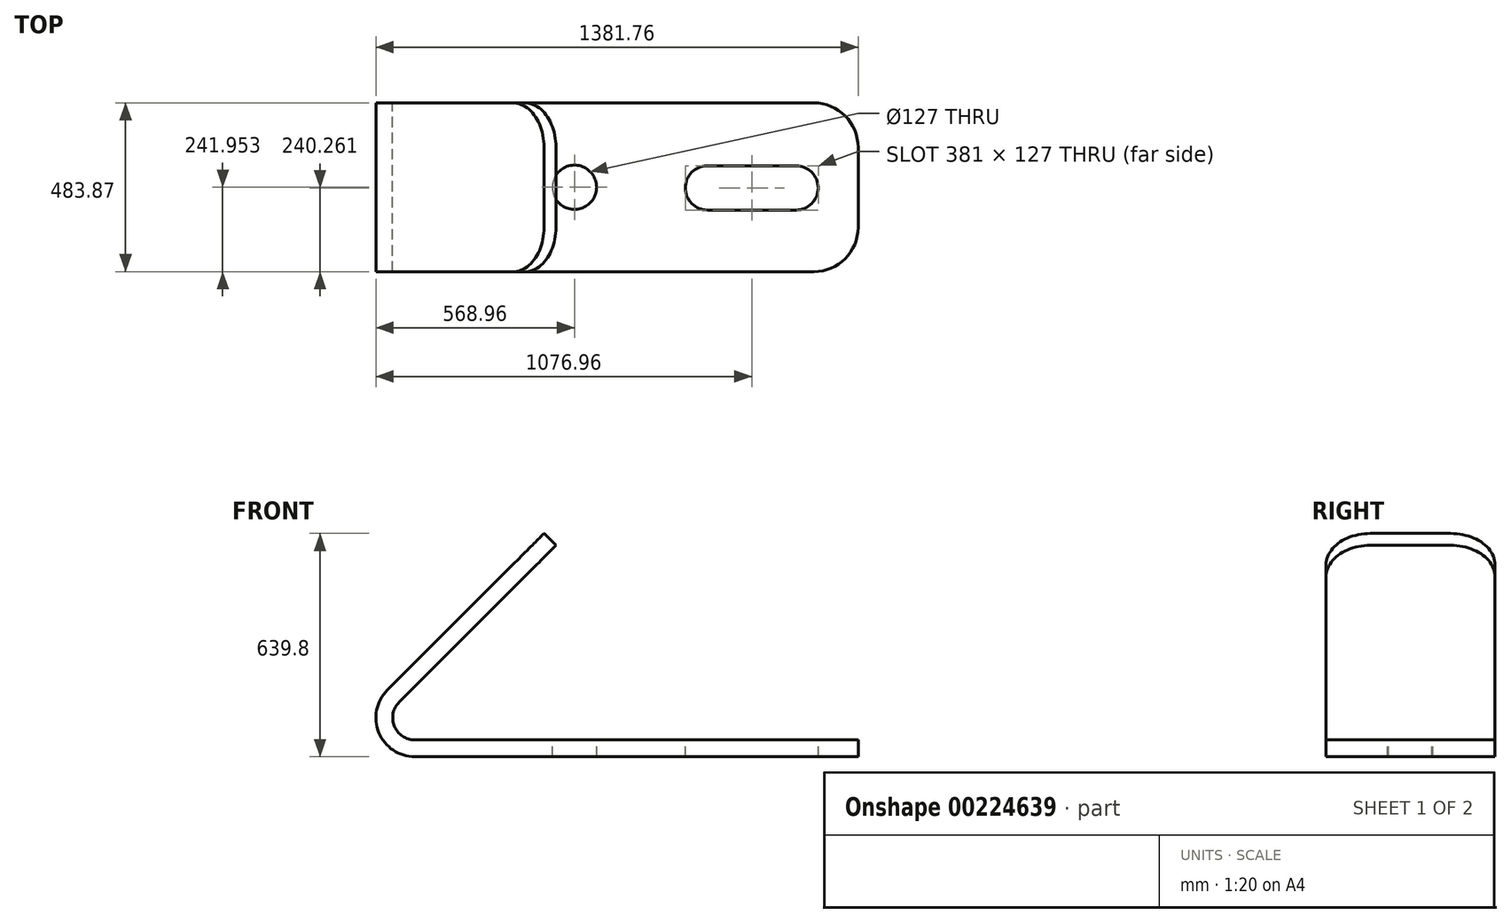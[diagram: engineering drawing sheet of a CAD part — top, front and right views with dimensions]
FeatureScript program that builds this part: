
annotation { "Feature Type Name" : "Feature", "Feature Type Description" : "" }
export const myFeature = defineFeature(function(context is Context, id is Id, definition is map)
    precondition{}
    {
        {
            var Q0;
            Q0=qCreatedBy(makeId("Front.planeOp"),FACE);
            var sketch = newSketch(context, id + "F0", { "sketchPlane" : qUnion([Q0])});
            skLineSegment(sketch, "E0", {"start": v(0, 0) * mm, "end": v(-1270, 0) * mm});
            skLineSegment(sketch, "E1", {"start": v(0, 0) * mm, "end": v(0, 48.26) * mm});
            skLineSegment(sketch, "E2", {"start": v(-1270, 48.26) * mm, "end": v(0, 48.26) * mm});
            skLineSegment(sketch, "E3", {"start": v(-1349.03, 190.79) * mm, "end": v(-900.01, 639.8) * mm});
            skArc(sketch, "E4", {"start": v(-1270, 0) * mm, "mid": v(-1373.25, 69) * mm, "end": v(-1349.03, 190.79) * mm});
            skLineSegment(sketch, "E5", {"start": v(-900.01, 639.8) * mm, "end": v(-865.89, 605.67) * mm});
            skLineSegment(sketch, "E6", {"start": v(-865.89, 605.67) * mm, "end": v(-1314.9, 156.66) * mm});
            skArc(sketch, "E7", {"start": v(-1270, 48.26) * mm, "mid": v(-1328.67, 87.46) * mm, "end": v(-1314.9, 156.66) * mm});
            skSolve(sketch);
        }
        {
            var Q0;
            Q0 = qSketchRegion(id + "F0", true);
            extrude(context, id + "F1", {"entities" : qUnion([Q0]), "depth" : 483.87 * mm});
        }
        {
            var Q0;
            Q0=makeQuery(id+"F1.opExtrude","CAP_EDGE",EDGE,{"disambiguationData":[OSD([sQuery(id+"F0.wireOp",EDGE,"E5")])],"isStart":true});
            var Q1;
            Q1=makeQuery(id+"F1.opExtrude","CAP_EDGE",EDGE,{"disambiguationData":[OSD([sQuery(id+"F0.wireOp",EDGE,"E5")])],"isStart":false});
            fillet(context, id + "F2", {"entities" : qUnion([Q0, Q1]), "radius" : 127 * mm, "tangentPropagation" : true, "allowEdgeOverflow" : false});
        }
        {
            var Q0;
            Q0=makeQuery(id+"F1.opExtrude","CAP_EDGE",EDGE,{"disambiguationData":[OSD([sQuery(id+"F0.wireOp",EDGE,"E1")])],"isStart":false});
            var Q1;
            Q1=makeQuery(id+"F1.opExtrude","CAP_EDGE",EDGE,{"disambiguationData":[OSD([sQuery(id+"F0.wireOp",EDGE,"E1")])],"isStart":true});
            fillet(context, id + "F3", {"entities" : qUnion([Q0, Q1]), "radius" : 127 * mm, "tangentPropagation" : true, "allowEdgeOverflow" : false});
        }
        {
            var Q0;
            Q0=makeQuery(id+"F1.opExtrude","SWEPT_FACE",FACE,{"disambiguationData":[OSD([sQuery(id+"F0.wireOp",EDGE,"E3")])]});
            var sketch = newSketch(context, id + "F4", { "sketchPlane" : qUnion([Q0])});
            skCircle(sketch, "E8", {"center": v(-374.5, -114.3) * mm, "radius": 38.1 * mm});
            skCircle(sketch, "E9", {"center": v(-374.5, -369.57) * mm, "radius": 38.1 * mm});
            skSolve(sketch);
        }
        {
            var Q0;
            Q0 = qSketchRegion(id + "F4", true);
            extrude(context, id + "F5", {"entities" : qUnion([Q0]), "operationType" : NewBodyOperationType.REMOVE, "oppositeDirection" : true, "depth" : 317.5 * mm});
        }
        {
            var Q0;
            Q0=makeQuery(id+"F1.opExtrude","SWEPT_FACE",FACE,{"disambiguationData":[OSD([sQuery(id+"F0.wireOp",EDGE,"E2")])]});
            var sketch = newSketch(context, id + "F6", { "sketchPlane" : qUnion([Q0])});
            skCircle(sketch, "E10", {"center": v(-812.8, -241.92) * mm, "radius": 63.5 * mm});
            skLineSegment(sketch, "E11", {"start": v(-431.8, -180.1) * mm, "end": v(-177.8, -180.1) * mm});
            skLineSegment(sketch, "E12", {"start": v(-431.8, -307.1) * mm, "end": v(-177.8, -307.1) * mm});
            skArc(sketch, "E13", {"start": v(-431.8, -180.1) * mm, "mid": v(-495.3, -243.6) * mm, "end": v(-431.8, -307.1) * mm});
            skArc(sketch, "E14", {"start": v(-177.8, -307.1) * mm, "mid": v(-114.3, -243.6) * mm, "end": v(-177.8, -180.1) * mm});
            skSolve(sketch);
        }
        {
            var Q0;
            Q0 = qSketchRegion(id + "F6", true);
            extrude(context, id + "F7", {"entities" : qUnion([Q0]), "operationType" : NewBodyOperationType.REMOVE, "oppositeDirection" : true, "depth" : 193.04 * mm});
        }
    });
